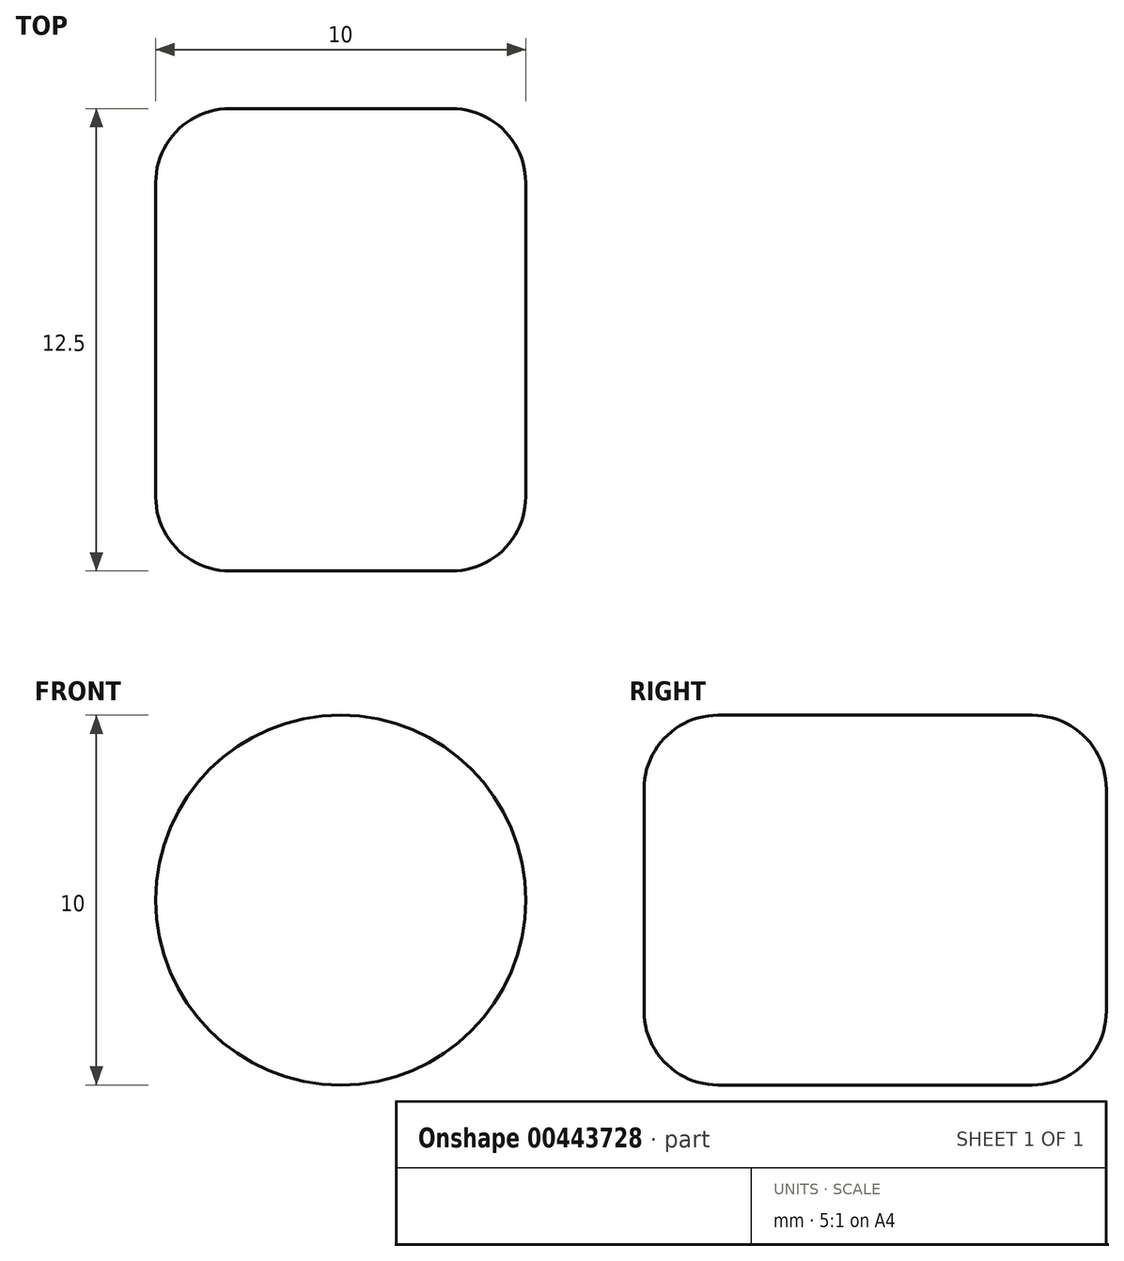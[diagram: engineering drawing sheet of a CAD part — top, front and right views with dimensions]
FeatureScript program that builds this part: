
annotation { "Feature Type Name" : "Feature", "Feature Type Description" : "" }
export const myFeature = defineFeature(function(context is Context, id is Id, definition is map)
    precondition{}
    {
        {
            var Q0;
            Q0=qCreatedBy(makeId("Front.planeOp"),FACE);
            var sketch = newSketch(context, id + "F0", { "sketchPlane" : qUnion([Q0])});
            skCircle(sketch, "E0", {"center": v(0, 0) * mm, "radius": 5 * mm});
            skSolve(sketch);
        }
        {
            var Q0;
            Q0=qSketchRegion(id+"F0",true);
            extrude(context, id + "F1", {"entities" : qUnion([Q0]), "depth" : 12.5 * mm});
        }
        {
            var Q0;
            Q0=makeQuery(id+"F1.opExtrude","CAP_FACE",FACE,{"disambiguationData":[OSD([sQuery(id+"F0.wireOp",EDGE,"E0")])],"isStart":false});
            var Q1;
            Q1=makeQuery(id+"F1.opExtrude","SWEPT_FACE",FACE,{"disambiguationData":[OSD([sQuery(id+"F0.wireOp",EDGE,"E0")])]});
            fillet(context, id + "F2", {"entities" : qUnion([Q0, Q1]), "radius" : 2 * mm, "tangentPropagation" : true, "allowEdgeOverflow" : false});
        }
    });
